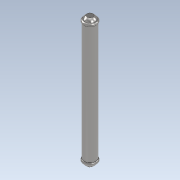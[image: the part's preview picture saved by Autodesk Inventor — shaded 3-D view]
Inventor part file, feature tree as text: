
AUTODESK INVENTOR PART (.ipt)
format: ipt  version: 2021 (Build 250183000, 183)  size: 112,640 bytes
history: native  units: mm
features: sketch x2, other x1, extrude x1, revolve x1, mirror x1
ambient origin geometry x8: Origin, YZ Plane, XZ Plane, XY Plane, X Axis, Y Axis, Z Axis, Center Point
bodies: Body1 (feature_tree)
feature tree (6):
  other  "Sólido1"
  extrude  "Extrusión1"  Depth=80.0mm TaperAngle=0.0deg
  revolve  "Revolución1"  [1 undecoded]
  mirror  "Simetría1"
  sketch  "Boceto1"  dims[d0=8.0mm d1=80.0mm d2=0.0mm]
  sketch  "Boceto2"  dims[d3=4.0mm d4=4.0mm d5=90.0deg d6=2.0mm d8=0.4mm]
note: 1 required parameter value undecoded (feature->parameter linkage not recoverable at this tier; creation-order binding heuristic only, values carry confidence <= 0.55)
